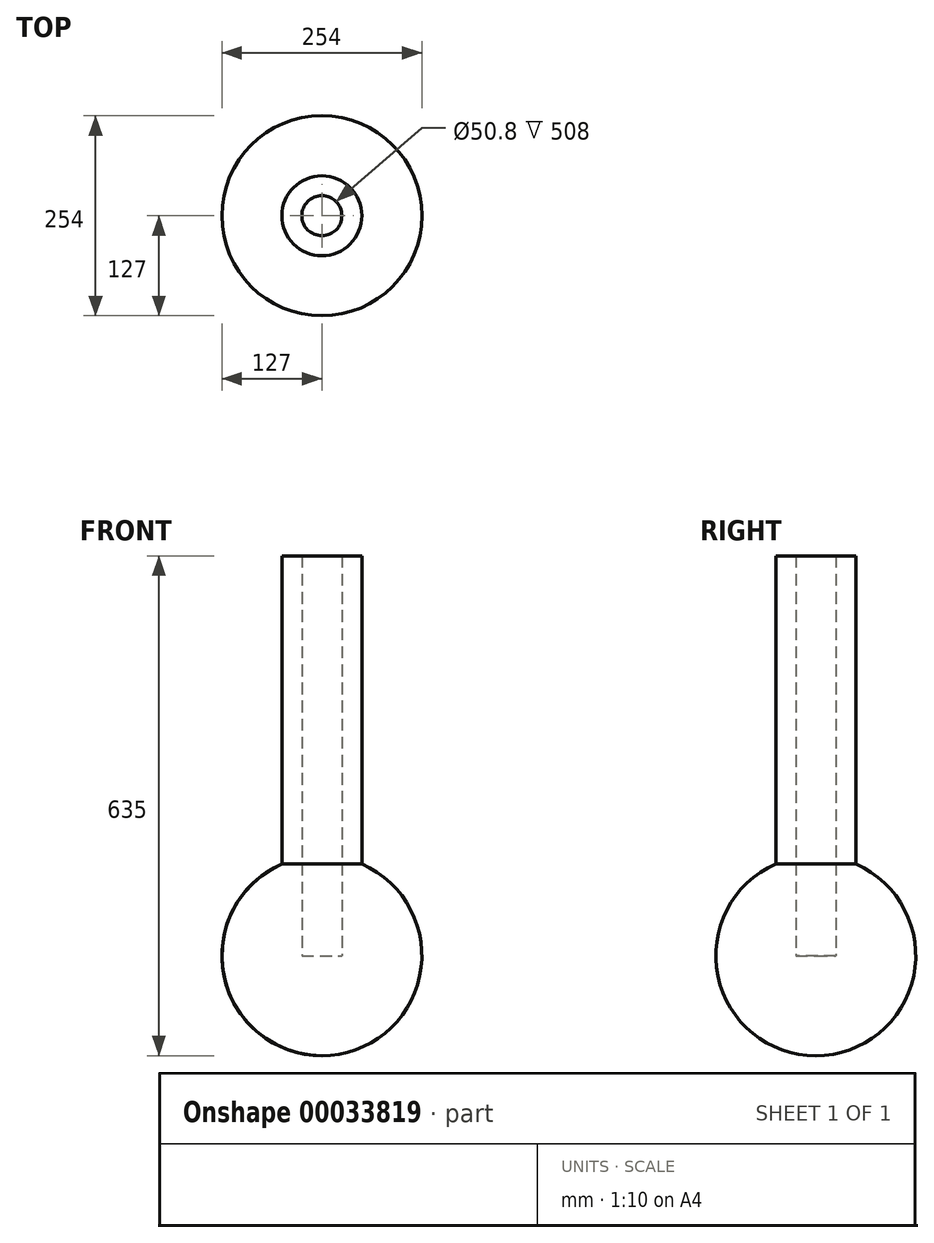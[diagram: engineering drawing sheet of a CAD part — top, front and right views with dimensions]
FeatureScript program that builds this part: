
annotation { "Feature Type Name" : "Feature", "Feature Type Description" : "" }
export const myFeature = defineFeature(function(context is Context, id is Id, definition is map)
    precondition{}
    {
        {
            var Q0;
            Q0=qCreatedBy(makeId("Front.planeOp"),FACE);
            var sketch = newSketch(context, id + "F0", { "sketchPlane" : qUnion([Q0])});
            skArc(sketch, "E0", {"start": v(-25.4, 124.43) * mm, "mid": v(-126.36, -12.76) * mm, "end": v(0, -127) * mm});
            skLineSegment(sketch, "E1.bottom", {"start": v(0, 0) * mm, "end": v(-50.8, 0) * mm});
            skLineSegment(sketch, "E1.top", {"start": v(0, 508) * mm, "end": v(-50.8, 508) * mm});
            skLineSegment(sketch, "E1.left", {"start": v(0, 0) * mm, "end": v(0, 127) * mm});
            skLineSegment(sketch, "E1.right", {"start": v(-50.8, 0) * mm, "end": v(-50.8, 508) * mm});
            skLineSegment(sketch, "E2.bottom", {"start": v(0, 0) * mm, "end": v(-25.4, 0) * mm});
            skLineSegment(sketch, "E2.top", {"start": v(0, 508) * mm, "end": v(-25.4, 508) * mm});
            skLineSegment(sketch, "E2.right", {"start": v(-25.4, 0) * mm, "end": v(-25.4, 508) * mm});
            skPoint(sketch, "E3", {"position": v(0, -127) * mm});
            skLineSegment(sketch, "E4", {"start": v(0, 0) * mm, "end": v(0, -127) * mm});
            skSolve(sketch);
        }
        {
            var Q0;
            Q0 = qSketchRegion(id + "F0", true);
            var Q1;
            Q1=sQuery(id+"F0.wireOp",EDGE,"E1.left");
            revolve(context, id + "F1", {"entities" : qUnion([Q0]), "axis" : qUnion([Q1]), "revolveType" : RevolveType.FULL});
        }
    });
